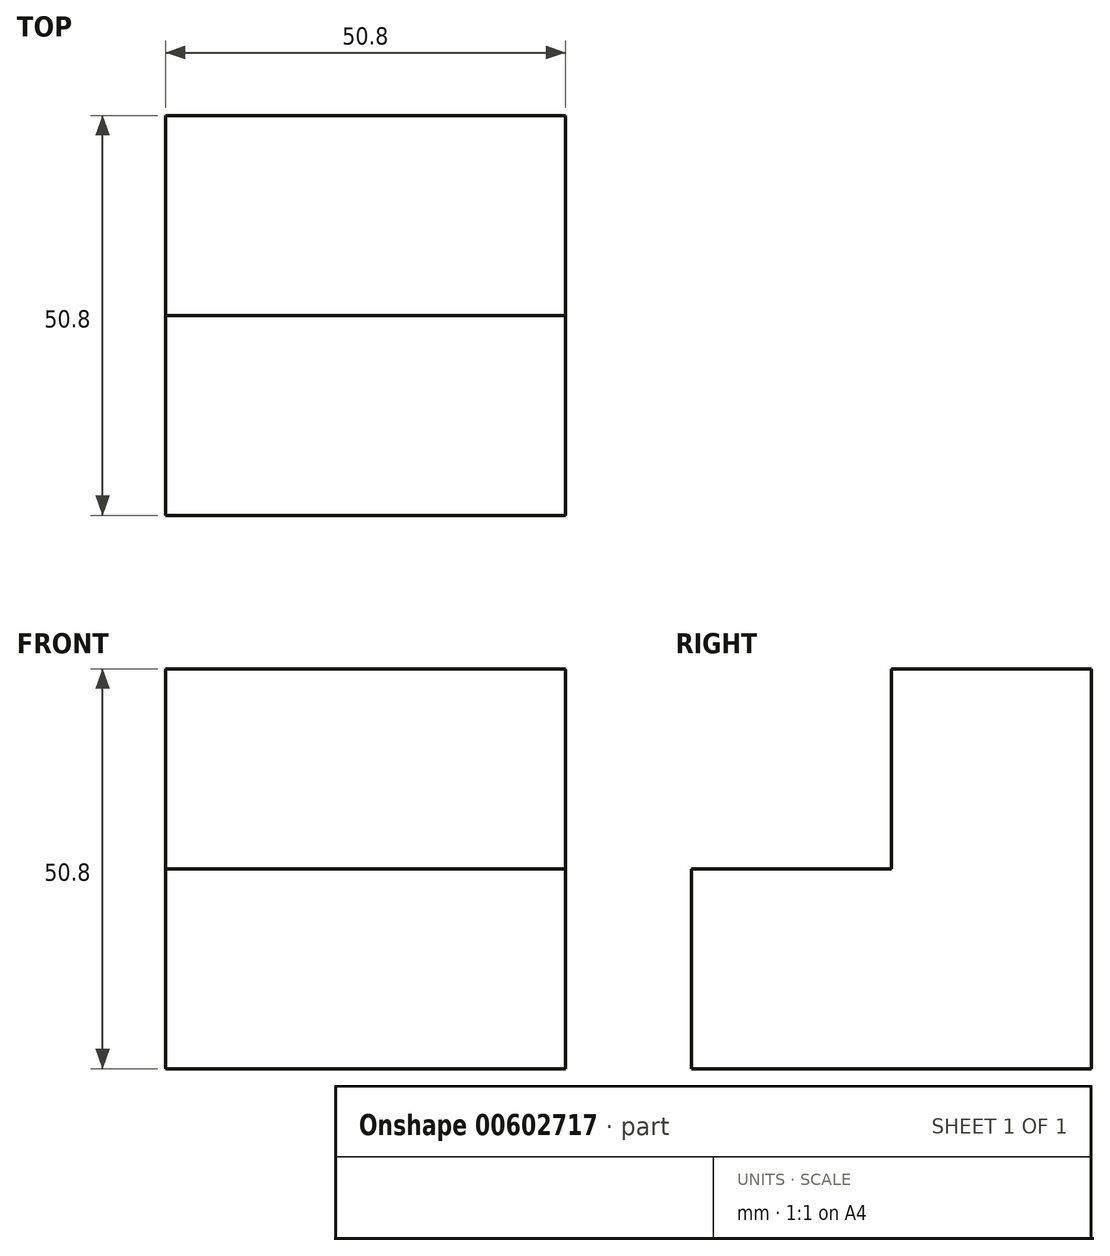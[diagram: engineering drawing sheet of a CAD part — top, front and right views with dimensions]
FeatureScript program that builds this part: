
annotation { "Feature Type Name" : "Feature", "Feature Type Description" : "" }
export const myFeature = defineFeature(function(context is Context, id is Id, definition is map)
    precondition{}
    {
        {
            var Q0;
            Q0=qCreatedBy(makeId("Front.planeOp"),FACE);
            var sketch = newSketch(context, id + "F0", { "sketchPlane" : qUnion([Q0])});
            skLineSegment(sketch, "E0", {"start": v(-48.67, 46.34) * mm, "end": v(-23.27, 46.34) * mm});
            skLineSegment(sketch, "E1", {"start": v(-23.27, 46.34) * mm, "end": v(-23.27, 20.94) * mm});
            skLineSegment(sketch, "E2", {"start": v(-23.27, 20.94) * mm, "end": v(-48.67, 20.94) * mm});
            skLineSegment(sketch, "E3", {"start": v(-48.67, 20.94) * mm, "end": v(-48.67, 46.34) * mm});
            skSolve(sketch);
        }
        {
            var Q0;
            Q0 = qSketchRegion(id + "F0", true);
            extrude(context, id + "F1", {"entities" : qUnion([Q0]), "depth" : 25.4 * mm, "offsetDistance" : 25.4 * mm});
        }
        {
            var Q0;
            Q0=makeQuery(id+"F1.opExtrude","CAP_FACE",FACE,{"disambiguationData":[OSD([sQuery(id+"F0.wireOp",EDGE,"E0"),sQuery(id+"F0.wireOp",EDGE,"E1"),sQuery(id+"F0.wireOp",EDGE,"E2"),sQuery(id+"F0.wireOp",EDGE,"E3")])],"isStart":false});
            var sketch = newSketch(context, id + "F2", { "sketchPlane" : qUnion([Q0])});
            skLineSegment(sketch, "E4", {"start": v(-48.67, 46.34) * mm, "end": v(-48.67, 20.94) * mm});
            skLineSegment(sketch, "E5", {"start": v(-48.67, 20.94) * mm, "end": v(-23.27, 20.94) * mm});
            skLineSegment(sketch, "E6", {"start": v(-23.27, 20.94) * mm, "end": v(-23.27, 46.34) * mm});
            skLineSegment(sketch, "E7", {"start": v(-23.27, 46.34) * mm, "end": v(-48.67, 46.34) * mm});
            skSolve(sketch);
        }
        {
            var Q0;
            Q0 = qSketchRegion(id + "F2", true);
            extrude(context, id + "F3", {"entities" : qUnion([Q0]), "operationType" : NewBodyOperationType.ADD, "depth" : 25.4 * mm, "offsetDistance" : 25.4 * mm});
        }
        {
            var Q0;
            Q0=makeQuery(id+"F3.boolean.opBoolean","MERGE",FACE,{"derivedFrom":[makeQuery(id+"F1.opExtrude","SWEPT_FACE",FACE,{"disambiguationData":[OSD([sQuery(id+"F0.wireOp",EDGE,"E1")])]}),makeQuery(id+"F3.opExtrude","SWEPT_FACE",FACE,{"disambiguationData":[OSD([sQuery(id+"F2.wireOp",EDGE,"E6")])]})]});
            var sketch = newSketch(context, id + "F4", { "sketchPlane" : qUnion([Q0])});
            skLineSegment(sketch, "E8", {"start": v(-50.8, 46.34) * mm, "end": v(0, 46.34) * mm});
            skLineSegment(sketch, "E9", {"start": v(0, 46.34) * mm, "end": v(0, 20.94) * mm});
            skLineSegment(sketch, "E10", {"start": v(0, 20.94) * mm, "end": v(-50.8, 20.94) * mm});
            skLineSegment(sketch, "E11", {"start": v(-50.8, 20.94) * mm, "end": v(-50.8, 46.34) * mm});
            skSolve(sketch);
        }
        {
            var Q0;
            Q0 = qSketchRegion(id + "F4", true);
            extrude(context, id + "F5", {"entities" : qUnion([Q0]), "operationType" : NewBodyOperationType.ADD, "depth" : 25.4 * mm, "offsetDistance" : 25.4 * mm});
        }
        {
            var Q0;
            Q0=makeQuery(id+"F5.boolean.opBoolean","MERGE",FACE,{"derivedFrom":[makeQuery(id+"F3.boolean.opBoolean","MERGE",FACE,{"derivedFrom":[makeQuery(id+"F1.opExtrude","SWEPT_FACE",FACE,{"disambiguationData":[OSD([sQuery(id+"F0.wireOp",EDGE,"E0")])]}),makeQuery(id+"F3.opExtrude","SWEPT_FACE",FACE,{"disambiguationData":[OSD([sQuery(id+"F2.wireOp",EDGE,"E7")])]})]}),makeQuery(id+"F5.opExtrude","SWEPT_FACE",FACE,{"disambiguationData":[OSD([sQuery(id+"F4.wireOp",EDGE,"E8")])]})]});
            var sketch = newSketch(context, id + "F6", { "sketchPlane" : qUnion([Q0])});
            skLineSegment(sketch, "E12", {"start": v(-48.67, 0) * mm, "end": v(-48.67, -25.4) * mm});
            skLineSegment(sketch, "E13", {"start": v(-48.67, -25.4) * mm, "end": v(2.13, -25.4) * mm});
            skLineSegment(sketch, "E14", {"start": v(2.13, -25.4) * mm, "end": v(2.13, 0) * mm});
            skLineSegment(sketch, "E15", {"start": v(2.13, 0) * mm, "end": v(-48.67, 0) * mm});
            skSolve(sketch);
        }
        {
            var Q0;
            Q0 = qSketchRegion(id + "F6", true);
            extrude(context, id + "F7", {"entities" : qUnion([Q0]), "operationType" : NewBodyOperationType.ADD, "depth" : 25.4 * mm, "offsetDistance" : 25.4 * mm});
        }
    });
